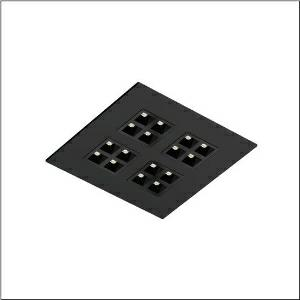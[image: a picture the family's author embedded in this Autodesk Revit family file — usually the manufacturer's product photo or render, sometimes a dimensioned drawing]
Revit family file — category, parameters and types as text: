
# Revit family: silica_r__31_square_51my6lmu44ba_567e
name_source: partatom
category: Lighting Fixtures
units: mm (PartAtom-declared; Revit-internal decimal feet)

## family parameters
Cut with Voids When Loaded = No
Host = Face
Light Source = No
Part Type = Normal
Room Calculation Point = No
Round Connector Dimension = Use Diameter
Shared = No

## types (1)
- --- (1 x LED, 6620 lm, 39 W, 4000K)
    Apparent Load = 39 VA
    CIE Flux Codes = 82 100 100 100 100
    Color Rendering = 80
    Color Temperature = 4000K
    Default Elevation = 1800 mm
    Description = Silica® 31 Square, office luminaire, primary light control with lens, of PMMA, primary anti-glare with reflector, of PC, black, light emission: direct distribution, primary light characteristic: symmetric, installation type: lay-in mounting, LED, rated luminous flux: 4.610lm, luminous efficacy: 177lm/W, light colour: 840, colour temperature: 4000K, control gear: ON/OFF Multilumen, with terminal, 3-pole, mains connection: 220..240V, AC, 50/60Hz, rated input power: 26W, luminaire housing, of sheet steel, coated, jet black (RAL 9005), module: M625, length: 620mm, width: 620mm, height: 43mm, protection rating (complete): IP20, insulation class (complete): insulation class II (safety insulation), certification: CE, impact resistance: IK03, permissible operating ambient temperature: -20..+35°C, standard: EN 50419, packaging unit: 1 piece
    Height = 0 mm  [stored 0 ft]
    Lamp = 1 x LED
    Lamp Light Flux = 6620 lm
    Lamp Power = 39 W
    Lamp count = 1
    Length = 620 mm
    Luminous efficacy = 170 lm/W
    Manufacturer = Siteco
    ModVariant = No
    Model = 51MY6LMU44BA
    Mounting Place = Ceiling
    Mounting Type = Recessed
    Number of Poles = 1
    OnlyDefault = Yes
    Power Factor = 1
    Product Name = Silica® 31 Square
    Product group = office luminaire | ceiling recessed
    ProductGroupID = 401
    Protection Class = Protection class II
    Protection Degree = IP 20
    RLX_Detail_Level = 1
    RLX_Emergency_Light_Flux = 0 lm
    RLX_Emergency_Type = 0
    RLX_Emergency_Type_DB = No
    RlxData = <blob elided: 36369 chars, md5=c5fb07b8>
    Socket = socket
    Standby Power = 0 W
    System Light Flux = 6620 lm
    System Power = 39 W
    Type Comments = factory setting: luminous flux: 100 % | (ON | ON | ON | ON) | 1100 mA
    Type Image = l_1313660.jpg
    URL = http://relux.com
    VarID = @adj_036296
    Voltage = 0 V
    Weight = 0.00 kg
    Width = 620 mm

note: [stored X ft] marks values corroborated as IEEE doubles in the binary element streams (Revit-internal decimal feet)

## geometry (parser evidence)
native form markers: Blend x4, Sweep x8
no freeform markers — native parametric forms only
